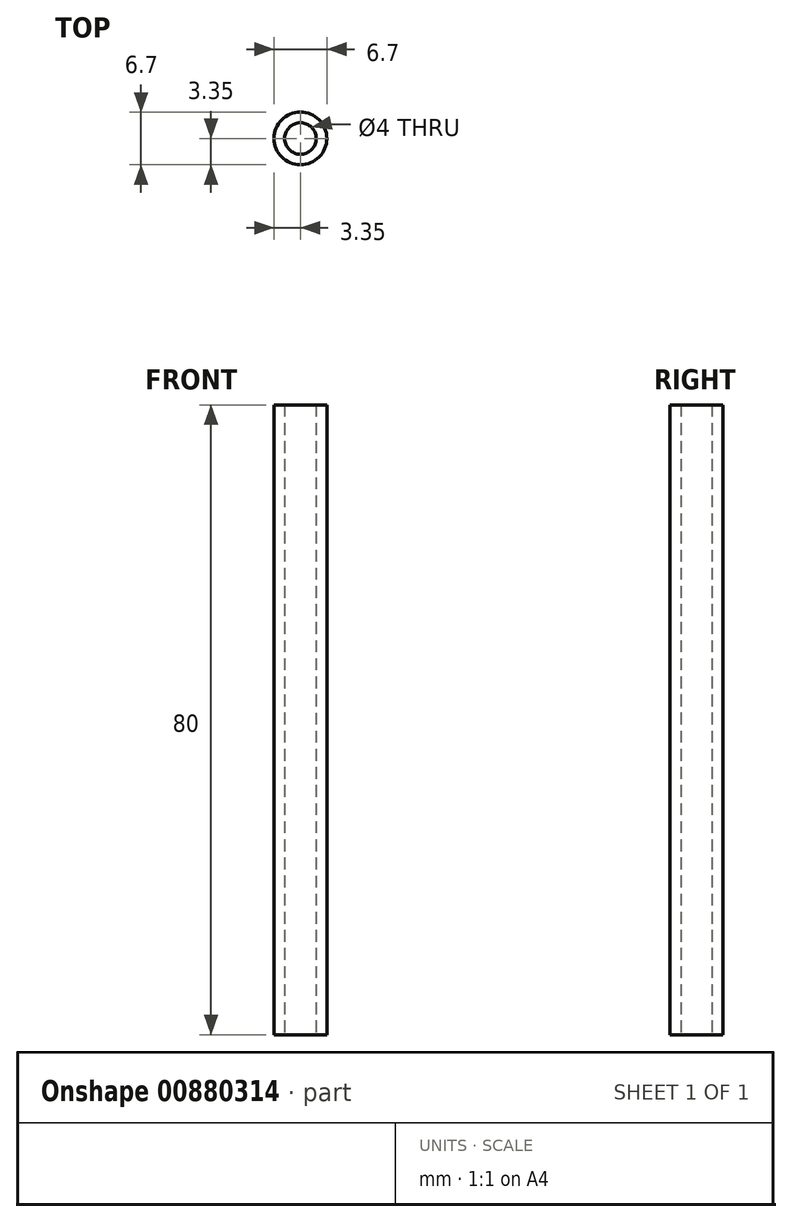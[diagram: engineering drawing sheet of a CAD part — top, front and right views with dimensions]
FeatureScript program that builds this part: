
annotation { "Feature Type Name" : "Feature", "Feature Type Description" : "" }
export const myFeature = defineFeature(function(context is Context, id is Id, definition is map)
    precondition{}
    {
        {
            var Q0;
            Q0=qCreatedBy(makeId("Top.planeOp"),FACE);
            var sketch = newSketch(context, id + "F0", { "sketchPlane" : qUnion([Q0])});
            skCircle(sketch, "E0", {"center": v(0, 0) * mm, "radius": 2 * mm});
            skCircle(sketch, "E1", {"center": v(0, 0) * mm, "radius": 3.35 * mm});
            skSolve(sketch);
        }
        {
            var Q0;
            Q0=makeQuery(id+"F0.imprint","IMPRINT",FACE,{"disambiguationData":[TD([[makeQuery(id+"F0.imprint","IMPRINT",EDGE,{"derivedFrom":sQuery(id+"F0.wireOp",EDGE,"E0")}),-1.0]])]});
            extrude(context, id + "F1", {"entities" : qUnion([Q0]), "depth" : 80 * mm, "offsetDistance" : 25.4 * mm});
        }
    });
